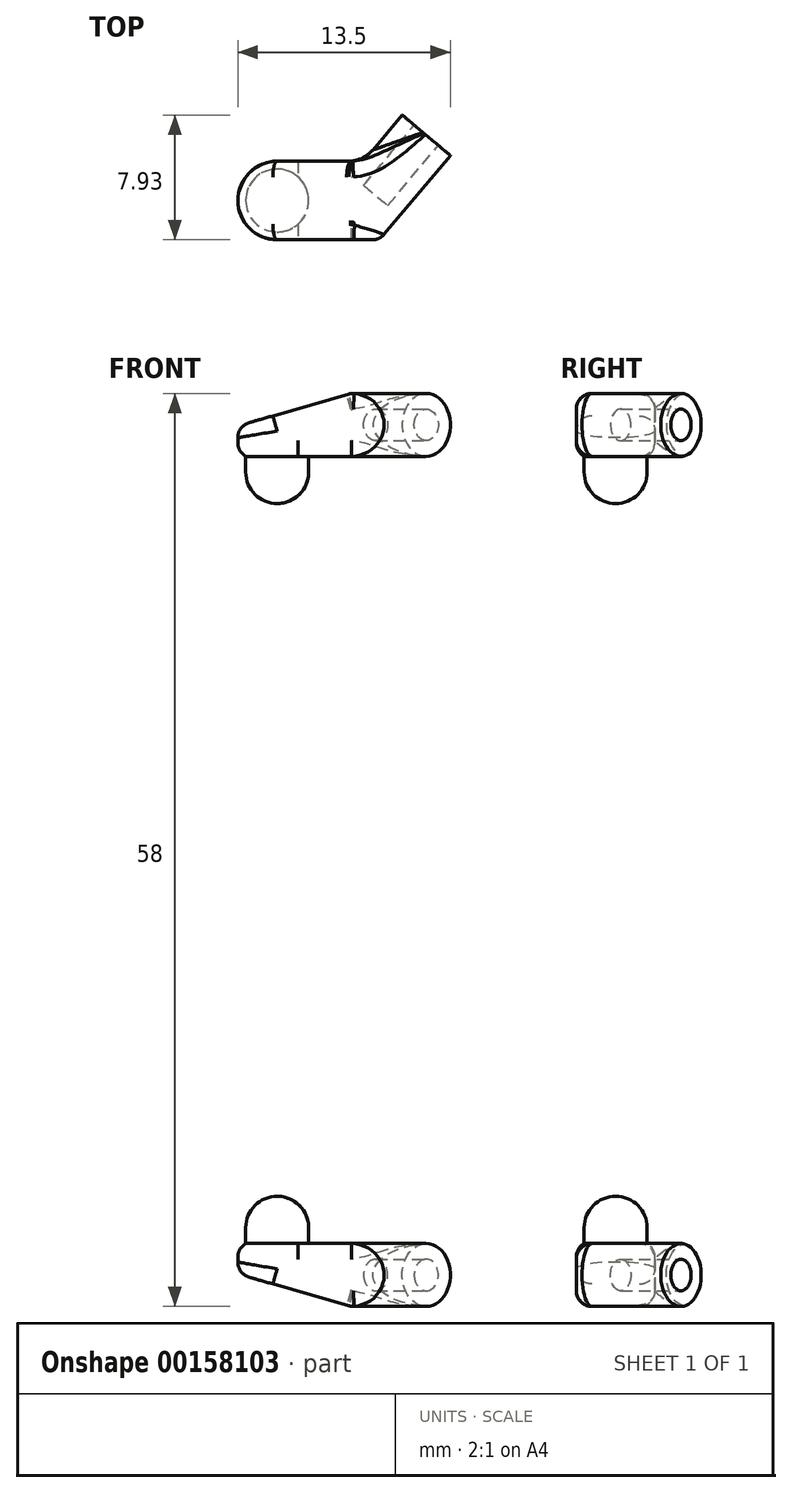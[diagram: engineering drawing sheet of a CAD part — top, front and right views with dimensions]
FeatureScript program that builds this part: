
annotation { "Feature Type Name" : "Feature", "Feature Type Description" : "" }
export const myFeature = defineFeature(function(context is Context, id is Id, definition is map)
    precondition{}
    {
        {
            var Q0;
            Q0=qCreatedBy(makeId("Top.planeOp"),FACE);
            var sketch = newSketch(context, id + "F0", { "sketchPlane" : qUnion([Q0])});
            skCircle(sketch, "E0", {"center": v(0, 0) * mm, "radius": 2 * mm});
            skSolve(sketch);
        }
        {
            var Q0;
            Q0=makeQuery(id+"F0.imprint","IMPRINT",FACE,{"disambiguationData":[TD([[makeQuery(id+"F0.imprint","IMPRINT",EDGE,{"derivedFrom":sQuery(id+"F0.wireOp",EDGE,"E0")}),1.0]])]});
            extrude(context, id + "F1", {"entities" : qUnion([Q0]), "depth" : 3 * mm});
        }
        {
            var Q0;
            Q0=makeQuery(id+"F1.opExtrude","CAP_FACE",FACE,{"disambiguationData":[OSD([sQuery(id+"F0.wireOp",EDGE,"E0")])],"isStart":false});
            var sketch = newSketch(context, id + "F2", { "sketchPlane" : qUnion([Q0])});
            skArc(sketch, "E1", {"start": v(0, 2.5) * mm, "mid": v(-2.5, 0) * mm, "end": v(0, -2.5) * mm});
            skLineSegment(sketch, "E2", {"start": v(0, 2.5) * mm, "end": v(5.47, 2.5) * mm});
            skPoint(sketch, "E3.start.orphan", {"position": v(0, -2.5) * mm});
            skLineSegment(sketch, "E4", {"start": v(6.5, -2.5) * mm, "end": v(0, -2.5) * mm});
            skLineSegment(sketch, "E5", {"start": v(6.5, -2.5) * mm, "end": v(11, 2.86) * mm});
            skLineSegment(sketch, "E6", {"start": v(11, 2.86) * mm, "end": v(7.94, 5.43) * mm});
            skLineSegment(sketch, "E7", {"start": v(7.94, 5.43) * mm, "end": v(5.47, 2.5) * mm});
            skSolve(sketch);
        }
        {
            var Q0;
            Q0=makeQuery(id+"F2.imprint","IMPRINT",FACE,{"disambiguationData":[TD([[makeQuery(id+"F2.imprint","IMPRINT",EDGE,{"derivedFrom":makeQuery(id+"F1.opExtrude","CAP_EDGE",EDGE,{"disambiguationData":[OSD([sQuery(id+"F0.wireOp",EDGE,"E0")])],"isStart":false})}),1.0]])]});
            var Q1;
            Q1=makeQuery(id+"F2.imprint","IMPRINT",FACE,{"disambiguationData":[TD([[makeQuery(id+"F2.imprint","IMPRINT",EDGE,{"derivedFrom":sQuery(id+"F2.wireOp",EDGE,"E1")}),1.0]])]});
            extrude(context, id + "F3", {"entities" : qUnion([Q0, Q1]), "operationType" : NewBodyOperationType.ADD, "depth" : 4 * mm});
        }
        {
            var Q0;
            Q0=makeQuery(id+"F3.opExtrude","CAP_EDGE",EDGE,{"disambiguationData":[OSD([sQuery(id+"F2.wireOp",EDGE,"E7")])],"isStart":false});
            var Q1;
            Q1=makeQuery(id+"F3.opExtrude","CAP_EDGE",EDGE,{"disambiguationData":[OSD([sQuery(id+"F2.wireOp",EDGE,"E7")])],"isStart":true});
            var Q2;
            Q2=makeQuery(id+"F3.opExtrude","CAP_EDGE",EDGE,{"disambiguationData":[OSD([sQuery(id+"F2.wireOp",EDGE,"E5")])],"isStart":false});
            var Q3;
            Q3=makeQuery(id+"F3.opExtrude","CAP_EDGE",EDGE,{"disambiguationData":[OSD([sQuery(id+"F2.wireOp",EDGE,"E5")])],"isStart":true});
            fillet(context, id + "F4", {"entities" : qUnion([Q0, Q1, Q2, Q3]), "radius" : 2 * mm, "tangentPropagation" : true, "allowEdgeOverflow" : false});
        }
        {
            var Q0;
            Q0=makeQuery(id+"F4.opFillet","BLEND_EDGE",EDGE,{"blendedFrom":[makeQuery(id+"F3.opExtrude","CAP_EDGE",EDGE,{"disambiguationData":[OSD([sQuery(id+"F2.wireOp",EDGE,"E7")])],"isStart":true}),makeQuery(id+"F3.opExtrude","SWEPT_FACE",FACE,{"disambiguationData":[OSD([sQuery(id+"F2.wireOp",EDGE,"E2")])]})],"blendedInto":[makeQuery(id+"F3.opExtrude","SWEPT_FACE",FACE,{"disambiguationData":[OSD([sQuery(id+"F2.wireOp",EDGE,"E2")])]})]});
            fillet(context, id + "F5", {"entities" : qUnion([Q0]), "radius" : 2 * mm, "tangentPropagation" : true, "allowEdgeOverflow" : false});
        }
        {
            var Q0;
            Q0=makeQuery(id+"F3.opExtrude","CAP_EDGE",EDGE,{"disambiguationData":[OSD([sQuery(id+"F2.wireOp",EDGE,"E1")])],"isStart":false});
            fillet(context, id + "F6", {"entities" : qUnion([Q0]), "radius" : 1 * mm, "tangentPropagation" : true, "allowEdgeOverflow" : false});
        }
        {
            var Q0;
            Q0=makeQuery(id+"F1.opExtrude","CAP_EDGE",EDGE,{"disambiguationData":[OSD([sQuery(id+"F0.wireOp",EDGE,"E0")])],"isStart":true});
            fillet(context, id + "F7", {"entities" : qUnion([Q0]), "radius" : 2 * mm, "tangentPropagation" : true, "allowEdgeOverflow" : false});
        }
        {
            var Q0;
            Q0=makeQuery(id+"F3.opExtrude","SWEPT_FACE",FACE,{"disambiguationData":[OSD([sQuery(id+"F2.wireOp",EDGE,"E6")])]});
            var sketch = newSketch(context, id + "F8", { "sketchPlane" : qUnion([Q0])});
            skCircle(sketch, "E8", {"center": v(-4.59, 5) * mm, "radius": 1 * mm});
            skSolve(sketch);
        }
        {
            var Q0;
            Q0=makeQuery(id+"F8.imprint","IMPRINT",FACE,{"disambiguationData":[TD([[makeQuery(id+"F8.imprint","IMPRINT",EDGE,{"derivedFrom":sQuery(id+"F8.wireOp",EDGE,"E8")}),1.0]])]});
            extrude(context, id + "F9", {"entities" : qUnion([Q0]), "operationType" : NewBodyOperationType.REMOVE, "oppositeDirection" : true, "depth" : 5 * mm});
        }
        {
            var Q0;
            Q0=makeQuery(id+"F3.opExtrude","SWEPT_FACE",FACE,{"disambiguationData":[OSD([sQuery(id+"F2.wireOp",EDGE,"E2")])]});
            var sketch = newSketch(context, id + "F10", { "sketchPlane" : qUnion([Q0])});
            skPoint(sketch, "E9.0", {"position": v(-4.7, 7) * mm});
            skLineSegment(sketch, "E10", {"start": v(2.5, 6) * mm, "end": v(2.5, 3.87) * mm});
            skLineSegment(sketch, "E11", {"start": v(-4.7, 7) * mm, "end": v(2.5, 4.93) * mm});
            skLineSegment(sketch, "E12", {"start": v(2.5, 4.93) * mm, "end": v(3.57, 8.65) * mm});
            skLineSegment(sketch, "E13", {"start": v(3.57, 8.65) * mm, "end": v(-4.7, 7) * mm});
            skSolve(sketch);
        }
        {
            var Q0;
            {var subQ1=sQuery(id+"F10.wireOp",EDGE,"E12");Q0=makeQuery(id+"F10.imprint","IMPRINT",FACE,{"disambiguationData":[TD([[makeQuery(id+"F10.imprint","IMPRINT",EDGE,{"derivedFrom":subQ1}),1.0]])]});}
            var Q1;
            {var subQ0=sQuery(id+"F10.wireOp",EDGE,"E11");var subQ1=sQuery(id+"F2.wireOp",EDGE,"E2");var subQ2=makeQuery(id+"F6.opFillet","BLEND_EDGE",EDGE,{"blendedFrom":[makeQuery(id+"F3.opExtrude","CAP_EDGE",EDGE,{"disambiguationData":[OSD([subQ1])],"isStart":false}),makeQuery(id+"F3.opExtrude","SWEPT_FACE",FACE,{"disambiguationData":[OSD([subQ1])]})],"blendedInto":[makeQuery(id+"F3.opExtrude","SWEPT_FACE",FACE,{"disambiguationData":[OSD([subQ1])]})]});var subQ3=makeQuery(id+"F10.imprint","INTERSECT",VERTEX,{"derivedFrom":[subQ2,subQ0]});Q1=makeQuery(id+"F10.imprint","IMPRINT",FACE,{"disambiguationData":[TD([[makeQuery(id+"F10.imprint","IMPRINT",EDGE,{"disambiguationData":[TD([[subQ3,-1.0]])],"derivedFrom":subQ0}),1.0]])]});}
            extrude(context, id + "F11", {"entities" : qUnion([Q0, Q1]), "operationType" : NewBodyOperationType.REMOVE, "oppositeDirection" : true, "depth" : 20 * mm});
        }
        {
            var Q0;
            {var subQ0=sQuery(id+"F2.wireOp",EDGE,"E2");Q0=makeQuery(id+"F11.boolean.opBoolean","INTERSECT",EDGE,{"derivedFrom":[makeQuery(id+"F6.opFillet","BLEND_FACE",FACE,{"disambiguationData":[OSD([subQ0]),TDD([makeQuery(id+"F3.opExtrude","CAP_EDGE",EDGE,{"disambiguationData":[OSD([subQ0])],"isStart":false})])]}),makeQuery(id+"F11.opExtrude","SWEPT_FACE",FACE,{"disambiguationData":[OSD([sQuery(id+"F10.wireOp",EDGE,"E11")])]})]});}
            fillet(context, id + "F12", {"entities" : qUnion([Q0]), "radius" : 1 * mm, "tangentPropagation" : true, "allowEdgeOverflow" : false});
        }
        {
            var Q0;
            Q0=makeQuery(id+"F2.imprint","IMPRINT",FACE,{"disambiguationData":[TD([[makeQuery(id+"F2.imprint","IMPRINT",EDGE,{"derivedFrom":sQuery(id+"F2.wireOp",EDGE,"E1")}),1.0]])]});
            cPlane(context, id + "F13", {"entities" : qUnion([Q0]), "cplaneType" : CPlaneType.OFFSET, "offset" : 25 * mm, "oppositeDirection" : true, "width" : 150 * mm, "height" : 150 * mm});
        }
        {
            var Q0;
            Q0=makeQuery(id+"F1.opExtrude","SWEPT_BODY",BODY,{"disambiguationData":[OSD([sQuery(id+"F0.wireOp",EDGE,"E0")])]});
            var Q1;
            Q1=qCreatedBy(id+"F13.planeOp",FACE);
            mirror(context, id + "F14", {"entities" : qUnion([Q0]), "mirrorPlane" : qUnion([Q1])});
        }
    });
